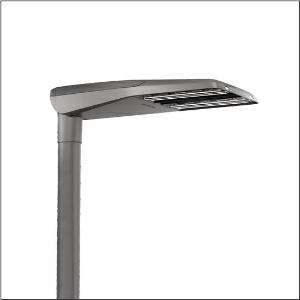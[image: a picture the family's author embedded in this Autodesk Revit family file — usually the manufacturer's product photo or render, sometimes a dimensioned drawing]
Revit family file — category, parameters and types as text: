
# Revit family: streetlight_sl_11_iq_midi___st1_0a_5xc3m51f08me_eb90
name_source: partatom
category: Lighting Fixtures
units: mm (PartAtom-declared; Revit-internal decimal feet)

## family parameters
Cut with Voids When Loaded = No
Host = Face
Light Source = No
Part Type = Normal
Room Calculation Point = No
Round Connector Dimension = Use Diameter
Shared = No

## types (1)
- --- (1 x LED, 17550 lm, 124.7 W, 3000K)
    Apparent Load = 125 VA
    CIE Flux Codes = 33 66 96 100 100
    Color Rendering = 70
    Color Temperature = 3000K
    Default Elevation = 1800 mm
    Description = Streetlight SL 11 iQ midi, mast luminaire, primary light control with 3 zone facetted reflector, of plastic, silver coated, highly specular, primary optical cover: cover, of PMMA, transparent, light distribution: ST1.0a, light emission: direct distribution, primary light characteristic: asymmetric, installation type: post-top, side-entry, LED, High Power LED, rated luminous flux: 17.550lm, luminous efficacy: 141lm/W, light colour: 730, colour temperature: 3000K, control: optimised constant luminous flux control (CLO 2.0), Street-Remote, Desk-Remote (wireless, voltage-free reading and setting of iQ features in the workshop via application-optimized NFC function/RFID function), Light-Fading, Smart-Wire, Night-Set, Lumen-Switch, Temp-Guard, Auto-Match, with cable H07RN-F 5x 1.5mm², mains connection: 230..240V, AC, 50/60Hz, connection cable pre-assembled, cable length: 12,5m, start of lifetime: 125W, end of service life: 132W, reduction: 57W, luminaire housing, of diecast aluminium, powder-coated, Siteco® metallic grey (DB 702S), please order mast flange separately, inclination adjustable without tools: 0°, 5°, 10°, 15° (post-top) | 0°, -5°, -10°, -15° (side-entry), sealing non-destructively replaceable, multi-level sealing system, length: 780mm, width: 376mm, height: 118mm, mast flange for spigot size: 42mm (side-entry): 5XC10008XM4, 60/48mm (side-entry/post-top): 5XC10108XM2, 76/60mm (side-entry/post-top): 5XC10108XM1, equipment: Power, protection rating (complete): IP66, insulation class (complete): insulation class II (safety insulation), certification: CE, ENEC, VDE, impact resistance: IK09, permissible operating ambient temperature for outdoor applications: -25..+50°C, standard-compliant lighting for roads and squares, Environmental Product Declaration (EPD) tested and certified by an independent institute, packaging unit: 1 piece

Light Distribution: ST1.0a
    Height = 118 mm
    Lamp = 1 x LED
    Lamp Light Flux = 17550 lm
    Lamp Power = 124.7 W
    Lamp count = 1
    Length = 780 mm
    Luminous efficacy = 141 lm/W
    Manufacturer = Siteco
    ModVariant = No
    Model = 5XC3M51F08ME
    Number of Poles = 1
    OnlyDefault = Yes
    Power Factor = 1
    Product Name = Streetlight SL 11 iQ midi | ST1.0a
    Product group = mast luminaire | pylon top
    ProductGroupID = 6100
    Protection Class = Protection class II
    Protection Degree = IP 66
    RLX_Detail_Level = 1
    RLX_Emergency_Light_Flux = 0 lm
    RLX_Emergency_Type = 0
    RLX_Emergency_Type_DB = No
    RlxData = <blob elided: 70201 chars, md5=726efb49>
    Socket = socket
    Standby Power = 0 W
    System Light Flux = 17550 lm
    System Power = 125 W
    Type Comments = factory setting: luminous flux: 100 % | dim-lin: 254 | 557 mA
    Type Image = l_1005960.jpg
    URL = http://relux.com
    VarID = @adj_039455
    Voltage = 0 V
    Weight = 0.00 kg
    Width = 376 mm

## geometry (parser evidence)
native form markers: Blend x4, Sweep x11
no freeform markers — native parametric forms only
